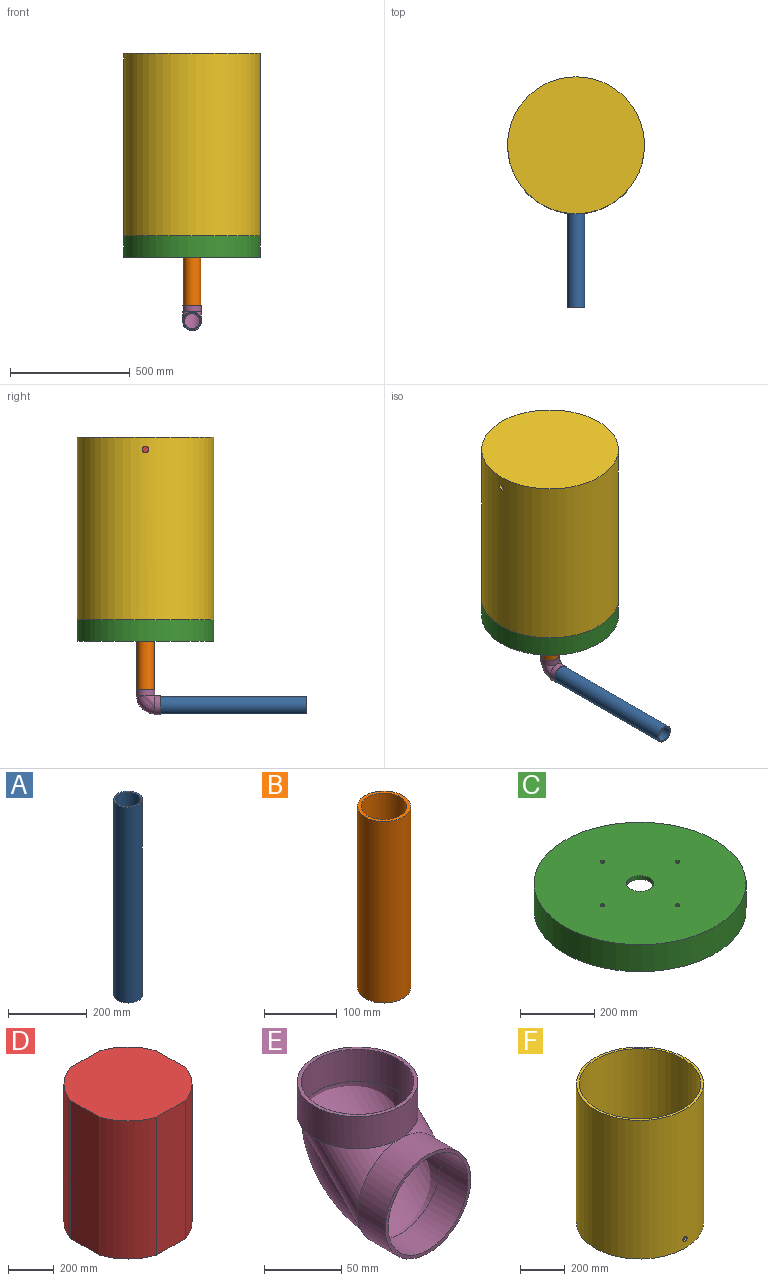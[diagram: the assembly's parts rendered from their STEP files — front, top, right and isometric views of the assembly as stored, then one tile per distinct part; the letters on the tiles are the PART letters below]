
ASSEMBLY  parts=6 mates=5
PART A: 4 faces, bbox 73x73x609.6 mm
  f0: cylinder r=31.36mm len=609.6mm, axis (0,0,-1), area 120101.8mm2, adj f2,f3
  f1: cylinder r=36.51mm len=609.6mm, axis (0,0,-1), area 139851.3mm2, adj f2,f3
  f2: plane 73.03x73.03mm, normal (0,0,1), area 1099.4mm2, adj f0,f1
  f3: plane 73.03x73.03mm, normal (0,0,-1), area 1099.4mm2, adj f0,f1
PART B: 4 faces, bbox 73x73x304.8 mm
  f0: cylinder r=31.36mm len=304.8mm, axis (0,0,-1), area 60050.9mm2, adj f2,f3
  f1: cylinder r=36.51mm len=304.8mm, axis (0,0,-1), area 69925.6mm2, adj f2,f3
  f2: plane 73.03x73.03mm, normal (0,0,1), area 1099.4mm2, adj f0,f1
  f3: plane 73.03x73.03mm, normal (0,0,-1), area 1099.4mm2, adj f0,f1
PART C: 10 faces, bbox 571.5x571.5x88.9 mm
  f0: cylinder r=6.35mm len=12.7mm, axis (0,0,-1), area 506.7mm2, adj f5,f8
  f1: cylinder r=6.35mm len=12.7mm, axis (0,0,-1), area 506.7mm2, adj f5,f8
  f2: cylinder r=6.35mm len=12.7mm, axis (0,0,-1), area 506.7mm2, adj f5,f8
  f3: cylinder r=6.35mm len=12.7mm, axis (0,0,-1), area 506.7mm2, adj f5,f8
  f4: cylinder r=285.75mm len=571.5mm, axis (0,0,-1), area 159612.9mm2, adj f5,f6
  f5: plane 571.5x571.5mm, normal (0,0,1), area 251825.7mm2, adj f0,f1,f2,f3,f4,f9
  f6: plane 571.5x571.5mm, normal (0,0,-1), area 22295.1mm2, adj f4,f7
  f7: cylinder r=273.05mm len=546.1mm, axis (0,0,-1), area 130730.5mm2, adj f6,f8
  f8: plane 546.1x546.1mm, normal (0,0,-1), area 229530.6mm2, adj f0,f1,f2,f3,f7,f9
  f9: cylinder r=36.51mm len=73.03mm, axis (0,0,1), area 2913.6mm2, adj f5,f8
PART D: 10 faces, bbox 529.6x529.6x736.6 mm
  f0: cylinder r=279.4mm len=736.6mm, axis (0,0,-1), area 189620.6mm2, adj f4,f5,f6,f9
  f1: cylinder r=279.4mm len=736.6mm, axis (0,0,-1), area 189620.6mm2, adj f4,f5,f8,f9
  f2: cylinder r=279.4mm len=736.6mm, axis (0,0,-1), area 189620.6mm2, adj f4,f5,f7,f8
  f3: cylinder r=279.4mm len=736.6mm, axis (0,0,-1), area 189620.6mm2, adj f4,f5,f6,f7
  f4: plane 529.6x529.6mm, normal (0,0,1), area 238267.5mm2, adj f0,f1,f2,f3,f6,f7,f8,f9
  f5: plane 529.6x529.6mm, normal (0,0,-1), area 238267.5mm2, adj f0,f1,f2,f3,f6,f7,f8,f9
  f6: plane 736.6x178.28mm, normal (1,0,0), area 131322.2mm2, adj f0,f3,f4,f5
  f7: plane 736.6x178.28mm, normal (0,-1,0), area 131322.2mm2, adj f2,f3,f4,f5
  f8: plane 736.6x178.28mm, normal (-1,0,0), area 131322.2mm2, adj f1,f2,f4,f5
  f9: plane 736.6x178.28mm, normal (0,1,0), area 131322.2mm2, adj f0,f1,f4,f5
PART E: 8 faces, bbox 78.2x110x169.2 mm
  f0: torus R=39.09mm, axis (-1,0,0), area 14086.8mm2, adj f2,f5
  f1: torus R=39.09mm, axis (-1,0,0), area 15081.5mm2, adj f4,f7
  f2: cylinder r=36.51mm len=73.03mm, axis (0,0,1), area 5827.1mm2, adj f0,f3
  f3: plane 78.18x78.18mm, normal (0,0,-1), area 612.3mm2, adj f2,f4
  f4: cylinder r=39.09mm len=78.18mm, axis (0,0,1), area 6238.6mm2, adj f1,f3
  f5: cylinder r=36.51mm len=73.03mm, axis (0,-1,0), area 5827.1mm2, adj f0,f6
  f6: plane 78.18x78.18mm, normal (0,1,0), area 612.3mm2, adj f5,f7
  f7: cylinder r=39.09mm len=78.18mm, axis (0,-1,0), area 6238.6mm2, adj f1,f6
PART F: 6 faces, bbox 571.5x571.5x762 mm
  f0: cylinder r=285.75mm len=762mm, axis (0,0,-1), area 1367549.9mm2, adj f2,f3,f5
  f1: cylinder r=273.05mm len=749.3mm, axis (0,0,-1), area 1284956.6mm2, adj f2,f4,f5
  f2: plane 571.5x571.5mm, normal (0,0,1), area 22295.1mm2, adj f0,f1
  f3: plane 571.5x571.5mm, normal (0,0,-1), area 256520.7mm2, adj f0
  f4: plane 546.1x546.1mm, normal (0,0,1), area 234225.5mm2, adj f1
  f5: cylinder r=13.33mm len=26.67mm, axis (0,1,0), area 1064.7mm2, adj f0,f1
PLACE A rot(axis=(1,0,0),90deg) t=(-1139.42,-763.87,-648.23)mm
PLACE B rot(axis=(0,1,0),180deg) t=(-1139.42,-699.38,-278.94)mm
PLACE C rot(axis=(0.71,0.71,0),180deg) t=(-1139.42,-699.38,-291.64)mm
PLACE D t=(-1139.42,-699.38,-278.94)mm
PLACE E t=(-1139.42,-699.38,-609.14)mm
PLACE F rot(axis=(-0.71,-0.71,0),180deg) t=(-1139.42,-699.38,470.36)mm
MATE fastened E.f2 <-> B.f0  axis (0,0,1) through (-1139.42,-699.38,-583.74)mm
MATE fastened D.f0 <-> B.f0  axis (0,0,-1) through (-1139.42,-699.38,-278.94)mm
MATE fastened F.f0 <-> C.f4  axis (0,0,-1) through (-1139.42,-699.38,-291.64)mm
MATE fastened A.f0 <-> E.f5  axis (0,1,0) through (-1139.42,-763.87,-648.23)mm
MATE fastened F.f0 <-> D.f0  axis (0,0,-1) through (-1139.42,-699.38,457.66)mm
